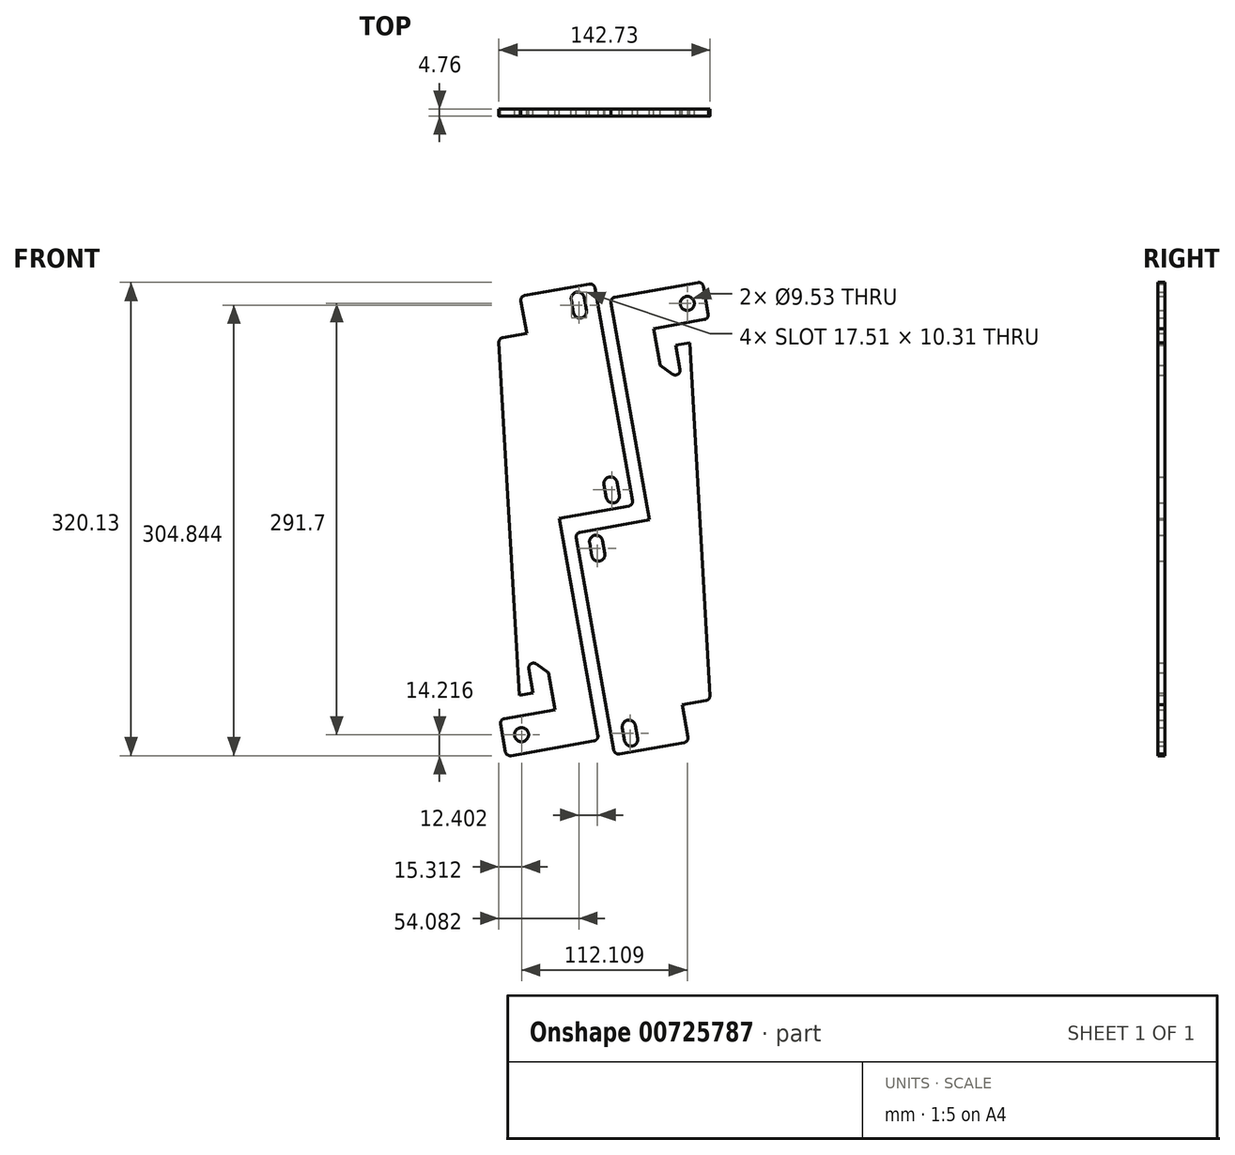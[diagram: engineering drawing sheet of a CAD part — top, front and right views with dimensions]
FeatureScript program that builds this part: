
annotation { "Feature Type Name" : "Feature", "Feature Type Description" : "" }
export const myFeature = defineFeature(function(context is Context, id is Id, definition is map)
    precondition{}
    {
        {
            var Q0;
            Q0=qCreatedBy(makeId("Front.planeOp"),FACE);
            var sketch = newSketch(context, id + "F0", { "sketchPlane" : qUnion([Q0])});
            skArc(sketch, "E0.MirrorCS", {"start": v(1.57, 25.06) * mm, "mid": v(2.1, 27.43) * mm, "end": v(4.14, 28.74) * mm});
            skArc(sketch, "E1.MirrorCS", {"start": v(71.7, 138.79) * mm, "mid": v(70.28, 135.56) * mm, "end": v(66.75, 135.63) * mm});
            skArc(sketch, "E2.MirrorCS", {"start": v(91.98, -81.82) * mm, "mid": v(91.3, -83.97) * mm, "end": v(89.36, -85.13) * mm});
            skArc(sketch, "E3.MirrorCS", {"start": v(34.3, -112.3) * mm, "mid": v(39.45, -115.9) * mm, "end": v(43.05, -110.75) * mm});
            skArc(sketch, "E4.MirrorCS", {"start": v(-50.74, 157.07) * mm, "mid": v(-50.07, 159.23) * mm, "end": v(-48.13, 160.38) * mm});
            skArc(sketch, "E5.MirrorCS", {"start": v(30.74, -121.32) * mm, "mid": v(28.36, -120.8) * mm, "end": v(27.06, -118.75) * mm});
            skArc(sketch, "E6.MirrorCS", {"start": v(10.5, 196.57) * mm, "mid": v(12.87, 196.05) * mm, "end": v(14.17, 194) * mm});
            skArc(sketch, "E7.MirrorCS", {"start": v(39.67, 50.2) * mm, "mid": v(39.14, 47.82) * mm, "end": v(37.1, 46.51) * mm});
            skArc(sketch, "E8.MirrorCS", {"start": v(-49.6, -101.06) * mm, "mid": v(-49.08, -98.69) * mm, "end": v(-47.03, -97.38) * mm});
            skArc(sketch, "E9.MirrorCS", {"start": v(-42.6, -122.4) * mm, "mid": v(-44.97, -121.87) * mm, "end": v(-46.28, -119.82) * mm});
            skArc(sketch, "E10.MirrorCS", {"start": v(16.24, -108.74) * mm, "mid": v(15.72, -111.1) * mm, "end": v(13.67, -112.42) * mm});
            skArc(sketch, "E11.MirrorCS", {"start": v(90.84, 176.31) * mm, "mid": v(90.31, 173.94) * mm, "end": v(88.27, 172.63) * mm});
            skArc(sketch, "E12.MirrorCS", {"start": v(83.83, 197.64) * mm, "mid": v(86.2, 197.12) * mm, "end": v(87.51, 195.07) * mm});
            skArc(sketch, "E13.MirrorCS", {"start": v(24.99, 183.99) * mm, "mid": v(25.51, 186.36) * mm, "end": v(27.56, 187.67) * mm});
            skArc(sketch, "E14.MirrorCS", {"start": v(6.93, 187.56) * mm, "mid": v(1.78, 191.16) * mm, "end": v(-1.82, 186) * mm});
            skArc(sketch, "E15.MirrorCS", {"start": v(12.13, 12.75) * mm, "mid": v(17.29, 9.15) * mm, "end": v(20.89, 14.3) * mm});
            skLineSegment(sketch, "E16.MirrorCS", {"start": v(58.31, 141.53) * mm, "end": v(66.75, 135.63) * mm});
            skArc(sketch, "E17.MirrorCS", {"start": v(-30.46, -63.53) * mm, "mid": v(-29.04, -60.3) * mm, "end": v(-25.52, -60.38) * mm});
            skArc(sketch, "E18.MirrorCS", {"start": v(19.34, 23.05) * mm, "mid": v(14.18, 26.65) * mm, "end": v(10.58, 21.5) * mm});
            skLineSegment(sketch, "E19.MirrorCS", {"start": v(10.58, 21.5) * mm, "end": v(12.13, 12.75) * mm});
            skArc(sketch, "E20.MirrorCS", {"start": v(77.08, -109.88) * mm, "mid": v(76.55, -112.25) * mm, "end": v(74.5, -113.56) * mm});
            skLineSegment(sketch, "E21.MirrorCS", {"start": v(32.75, -103.55) * mm, "end": v(34.3, -112.3) * mm});
            skLineSegment(sketch, "E22.MirrorCS", {"start": v(41.5, -102) * mm, "end": v(43.05, -110.75) * mm});
            skLineSegment(sketch, "E23.MirrorCS", {"start": v(19.34, 23.05) * mm, "end": v(20.89, 14.3) * mm});
            skArc(sketch, "E24.MirrorCS", {"start": v(-35.85, 185.13) * mm, "mid": v(-35.32, 187.5) * mm, "end": v(-33.27, 188.81) * mm});
            skLineSegment(sketch, "E25.MirrorCS", {"start": v(30.65, 53.75) * mm, "end": v(29.1, 62.5) * mm});
            skLineSegment(sketch, "E26.MirrorCS", {"start": v(68.79, 155.17) * mm, "end": v(78.2, 156.84) * mm});
            skLineSegment(sketch, "E27.MirrorCS", {"start": v(-17.08, -66.28) * mm, "end": v(-25.52, -60.38) * mm});
            skLineSegment(sketch, "E28.MirrorCS", {"start": v(-27.56, -79.92) * mm, "end": v(-36.97, -81.6) * mm});
            skLineSegment(sketch, "E29.MirrorCS", {"start": v(21.9, 52.2) * mm, "end": v(20.35, 60.95) * mm});
            skArc(sketch, "E30.MirrorCS", {"start": v(21.9, 52.2) * mm, "mid": v(27.05, 48.6) * mm, "end": v(30.65, 53.75) * mm});
            skLineSegment(sketch, "E31.MirrorCS", {"start": v(-0.27, 177.25) * mm, "end": v(-1.82, 186) * mm});
            skLineSegment(sketch, "E32.MirrorCS", {"start": v(8.48, 178.8) * mm, "end": v(6.93, 187.56) * mm});
            skArc(sketch, "E33.MirrorCS", {"start": v(29.1, 62.5) * mm, "mid": v(23.95, 66.1) * mm, "end": v(20.35, 60.95) * mm});
            skArc(sketch, "E34.MirrorCS", {"start": v(-0.27, 177.25) * mm, "mid": v(4.88, 173.65) * mm, "end": v(8.48, 178.8) * mm});
            skArc(sketch, "E35.MirrorCS", {"start": v(41.5, -102) * mm, "mid": v(36.35, -98.4) * mm, "end": v(32.75, -103.55) * mm});
            skLineSegment(sketch, "E36.MirrorCS", {"start": v(88.27, 172.63) * mm, "end": v(53.88, 166.54) * mm});
            skCircle(sketch, "E37.MirrorC", {"center": v(76.67, 183.48) * mm, "radius": 4.76 * mm});
            skPoint(sketch, "E38.MirrorP", {"position": v(6.09, -107.08) * mm});
            skLineSegment(sketch, "E39.MirrorCS", {"start": v(-46.28, -119.82) * mm, "end": v(-49.6, -101.06) * mm});
            skLineSegment(sketch, "E40.MirrorCS", {"start": v(27.56, 187.67) * mm, "end": v(83.83, 197.64) * mm});
            skPoint(sketch, "E41.MirrorP", {"position": v(-36.4, 188.26) * mm});
            skLineSegment(sketch, "E42.MirrorCS", {"start": v(-30.46, -63.53) * mm, "end": v(-27.56, -79.92) * mm});
            skLineSegment(sketch, "E43.MirrorCS", {"start": v(-9.8, 38.2) * mm, "end": v(16.24, -108.74) * mm});
            skLineSegment(sketch, "E44.MirrorCS", {"start": v(-31.97, 163.25) * mm, "end": v(-35.85, 185.13) * mm});
            skLineSegment(sketch, "E45.MirrorCS", {"start": v(-31.97, 163.25) * mm, "end": v(-48.13, 160.38) * mm});
            skLineSegment(sketch, "E46.MirrorCS", {"start": v(-12.64, -91.29) * mm, "end": v(-17.08, -66.28) * mm});
            skCircle(sketch, "E47.MirrorC", {"center": v(-35.44, -108.22) * mm, "radius": 4.76 * mm});
            skPoint(sketch, "E48.MirrorP", {"position": v(-45.73, -122.95) * mm});
            skPoint(sketch, "E49.MirrorP", {"position": v(91.4, 173.19) * mm});
            skLineSegment(sketch, "E50.MirrorCS", {"start": v(4.14, 28.74) * mm, "end": v(51.03, 37.05) * mm});
            skPoint(sketch, "E51.MirrorP", {"position": v(-0.08, 31.25) * mm});
            skPoint(sketch, "E52.MirrorP", {"position": v(-4.4, 25.1) * mm});
            skPoint(sketch, "E53.MirrorP", {"position": v(92.14, -84.64) * mm});
            skPoint(sketch, "E54.MirrorP", {"position": v(41.31, 44) * mm});
            skPoint(sketch, "E55.MirrorP", {"position": v(18.01, -117.25) * mm});
            skPoint(sketch, "E56.MirrorP", {"position": v(34.93, 54.92) * mm});
            skPoint(sketch, "E57.MirrorP", {"position": v(24.43, 187.11) * mm});
            skLineSegment(sketch, "E58.MirrorCS", {"start": v(27.06, -118.75) * mm, "end": v(1.57, 25.06) * mm});
            skLineSegment(sketch, "E59.MirrorCS", {"start": v(-50.74, 157.07) * mm, "end": v(-36.97, -81.6) * mm});
            skLineSegment(sketch, "E60.MirrorCS", {"start": v(73.2, -88) * mm, "end": v(77.08, -109.88) * mm});
            skPoint(sketch, "E61.MirrorP", {"position": v(86.96, 198.2) * mm});
            skLineSegment(sketch, "E62.MirrorCS", {"start": v(13.67, -112.42) * mm, "end": v(-42.6, -122.4) * mm});
            skLineSegment(sketch, "E63.MirrorCS", {"start": v(87.51, 195.07) * mm, "end": v(90.84, 176.31) * mm});
            skLineSegment(sketch, "E64.MirrorCS", {"start": v(-33.27, 188.81) * mm, "end": v(10.5, 196.57) * mm});
            skPoint(sketch, "E65.MirrorP", {"position": v(77.63, -113) * mm});
            skLineSegment(sketch, "E66.MirrorCS", {"start": v(-47.03, -97.38) * mm, "end": v(-12.64, -91.29) * mm});
            skLineSegment(sketch, "E67.MirrorCS", {"start": v(37.1, 46.51) * mm, "end": v(-9.8, 38.2) * mm});
            skLineSegment(sketch, "E68.MirrorCS", {"start": v(73.2, -88) * mm, "end": v(89.36, -85.13) * mm});
            skPoint(sketch, "E69.MirrorP", {"position": v(12.5, 197.28) * mm});
            skPoint(sketch, "E70.MirrorP", {"position": v(-50.9, 159.9) * mm});
            skLineSegment(sketch, "E71.MirrorCS", {"start": v(53.88, 166.54) * mm, "end": v(58.31, 141.53) * mm});
            skLineSegment(sketch, "E72.MirrorCS", {"start": v(51.03, 37.05) * mm, "end": v(24.99, 183.99) * mm});
            skPoint(sketch, "E73.MirrorP", {"position": v(-50.16, -97.94) * mm});
            skLineSegment(sketch, "E74.MirrorCS", {"start": v(71.7, 138.79) * mm, "end": v(68.79, 155.17) * mm});
            skPoint(sketch, "E75.MirrorP", {"position": v(27.61, -121.87) * mm});
            skLineSegment(sketch, "E76.MirrorCS", {"start": v(91.98, -81.82) * mm, "end": v(78.2, 156.84) * mm});
            skLineSegment(sketch, "E77.MirrorCS", {"start": v(14.17, 194) * mm, "end": v(39.67, 50.2) * mm});
            skLineSegment(sketch, "E78.MirrorCS", {"start": v(74.5, -113.56) * mm, "end": v(30.74, -121.32) * mm});
            skPoint(sketch, "E79.MirrorP", {"position": v(2.9, 201.9) * mm});
            skSolve(sketch);
        }
        {
            var Q0;
            Q0 = qSketchRegion(id + "F0", true);
            extrude(context, id + "F1", {"entities" : qUnion([Q0]), "flatOperationType" : FlatOperationType.REMOVE, "depth" : 4.76 * mm, "offsetDistance" : 25.4 * mm, "domain" : OperationDomain.MODEL});
        }
    });
